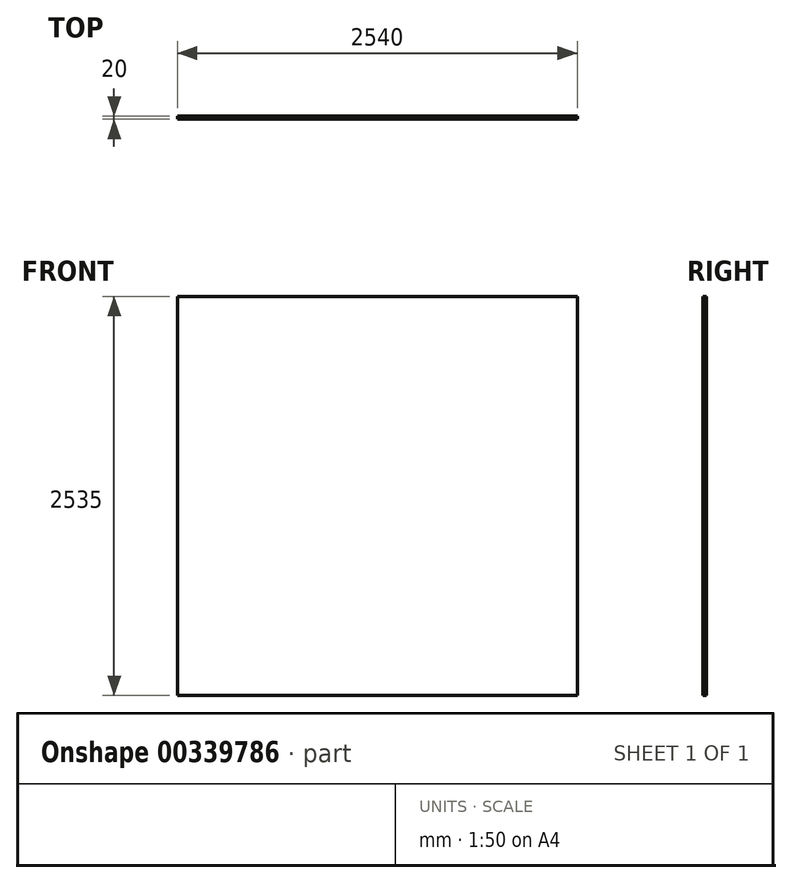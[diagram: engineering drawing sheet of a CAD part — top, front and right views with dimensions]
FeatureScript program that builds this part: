
annotation { "Feature Type Name" : "Feature", "Feature Type Description" : "" }
export const myFeature = defineFeature(function(context is Context, id is Id, definition is map)
    precondition{}
    {
        {
            var Q0;
            Q0=qCreatedBy(makeId("Front.planeOp"),FACE);
            var sketch = newSketch(context, id + "F0", { "sketchPlane" : qUnion([Q0])});
            skLineSegment(sketch, "E0.bottom", {"start": v(0, 0) * mm, "end": v(2540, 0) * mm});
            skLineSegment(sketch, "E0.top", {"start": v(0, 2535) * mm, "end": v(2540, 2535) * mm});
            skLineSegment(sketch, "E0.left", {"start": v(0, 0) * mm, "end": v(0, 2535) * mm});
            skLineSegment(sketch, "E0.right", {"start": v(2540, 0) * mm, "end": v(2540, 2535) * mm});
            skSolve(sketch);
        }
        {
            var Q0;
            Q0=makeQuery(id+"F0.imprint","IMPRINT",FACE,{"disambiguationData":[TD([[makeQuery(id+"F0.imprint","IMPRINT",EDGE,{"derivedFrom":sQuery(id+"F0.wireOp",EDGE,"E0.bottom")}),1.0]])]});
            extrude(context, id + "F1", {"entities" : qUnion([Q0]), "depth" : 20 * mm});
        }
    });
